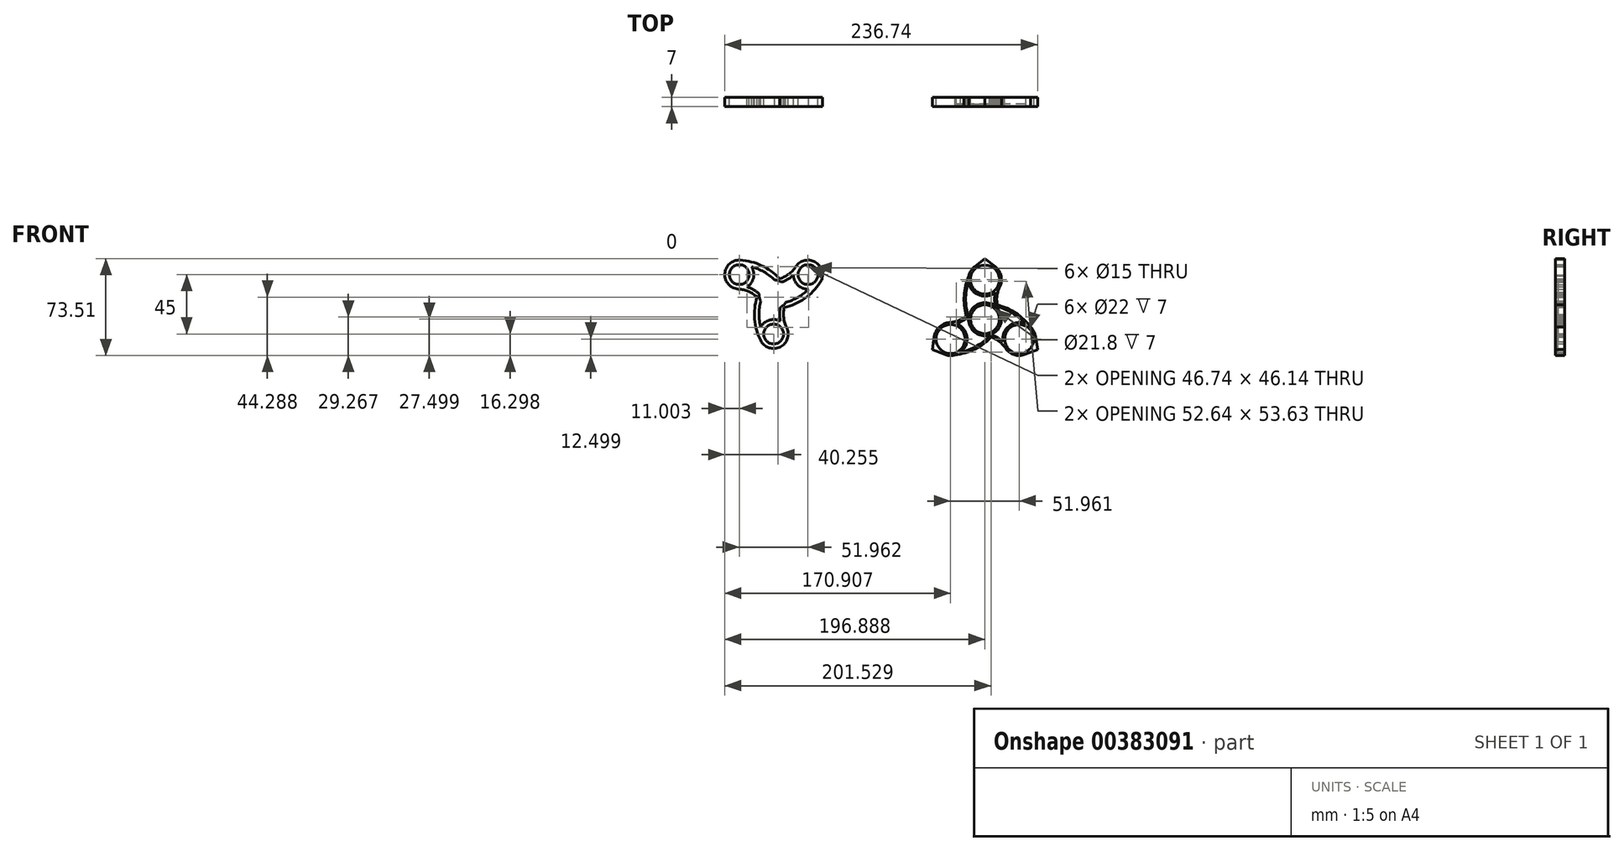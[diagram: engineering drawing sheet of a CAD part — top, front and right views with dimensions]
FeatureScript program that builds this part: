
annotation { "Feature Type Name" : "Feature", "Feature Type Description" : "" }
export const myFeature = defineFeature(function(context is Context, id is Id, definition is map)
    precondition{}
    {
        {
            var Q0;
            Q0=qCreatedBy(makeId("Front.planeOp"),FACE);
            var sketch = newSketch(context, id + "F0", { "sketchPlane" : qUnion([Q0])});
            skCircle(sketch, "E0", {"center": v(-54.28, -12.73) * mm, "radius": 11 * mm});
            skCircle(sketch, "E1", {"center": v(-54.28, -42.73) * mm, "radius": 11 * mm});
            skLineSegment(sketch, "E2", {"start": v(-54.28, 0) * mm, "end": v(-54.28, -55.46) * mm, "construction": true});
            skLineSegment(sketch, "E3", {"start": v(-54.28, -55.46) * mm, "end": v(-24.28, -27.73) * mm, "construction": true});
            skPoint(sketch, "E3.endSnap0", {"position": v(-54.28, -27.73) * mm});
            skLineSegment(sketch, "E4", {"start": v(-24.28, -27.73) * mm, "end": v(-54.28, 0) * mm, "construction": true});
            skLineSegment(sketch, "E5", {"start": v(-24.28, -27.73) * mm, "end": v(-54.28, -12.73) * mm, "construction": true});
            skLineSegment(sketch, "E6", {"start": v(-54.28, -12.73) * mm, "end": v(-87.47, 3.86) * mm, "construction": true});
            skLineSegment(sketch, "E7", {"start": v(-24.28, -27.73) * mm, "end": v(-54.28, -42.73) * mm, "construction": true});
            skLineSegment(sketch, "E8", {"start": v(-54.28, -42.73) * mm, "end": v(-98.2, -64.7) * mm, "construction": true});
            skArc(sketch, "E9", {"start": v(-64.12, -7.81) * mm, "mid": v(-68.82, -27.73) * mm, "end": v(-64.12, -47.65) * mm});
            skArc(sketch, "E10", {"start": v(-64.12, -17.65) * mm, "mid": v(-65.37, -27.73) * mm, "end": v(-64.12, -37.81) * mm});
            skArc(sketch, "E11", {"start": v(-49.17, -22.47) * mm, "mid": v(-49.72, -27.73) * mm, "end": v(-49.17, -32.99) * mm});
            skArc(sketch, "E12", {"start": v(-44.44, -17.65) * mm, "mid": v(-46.82, -27.73) * mm, "end": v(-44.44, -37.81) * mm});
            skCircle(sketch, "E13.1.0", {"center": v(-28.3, 2.27) * mm, "radius": 11 * mm});
            skArc(sketch, "E13.1.1", {"start": v(-45.1, -18.8) * mm, "mid": v(-35.74, -14.84) * mm, "end": v(-27.64, -8.71) * mm});
            skArc(sketch, "E13.1.2", {"start": v(-54.94, -1.75) * mm, "mid": v(-45.02, 1.23) * mm, "end": v(-37.48, 8.33) * mm});
            skArc(sketch, "E13.1.3", {"start": v(-53.62, -23.71) * mm, "mid": v(-34.02, -17.82) * mm, "end": v(-19.12, -3.8) * mm});
            skLineSegment(sketch, "E13.1.4", {"start": v(-65.3, -19.1) * mm, "end": v(-17.27, 8.63) * mm, "construction": true});
            skArc(sketch, "E13.1.5", {"start": v(-48.4, -3.44) * mm, "mid": v(-43.56, -1.28) * mm, "end": v(-39.29, 1.82) * mm});
            skPoint(sketch, "E13.1.7", {"position": v(-41.29, -5.23) * mm});
            skCircle(sketch, "E13.2.0", {"center": v(-80.26, 2.27) * mm, "radius": 11 * mm});
            skArc(sketch, "E13.2.1", {"start": v(-53.62, -1.75) * mm, "mid": v(-61.72, 4.38) * mm, "end": v(-71.08, 8.33) * mm});
            skArc(sketch, "E13.2.2", {"start": v(-63.46, -18.8) * mm, "mid": v(-71, -11.7) * mm, "end": v(-80.92, -8.71) * mm});
            skArc(sketch, "E13.2.3", {"start": v(-45.1, -6.67) * mm, "mid": v(-60, 7.36) * mm, "end": v(-79.6, 13.25) * mm});
            skLineSegment(sketch, "E13.2.4", {"start": v(-43.25, -19.1) * mm, "end": v(-91.28, 8.63) * mm, "construction": true});
            skArc(sketch, "E13.2.5", {"start": v(-65.27, -12.28) * mm, "mid": v(-69.55, -9.18) * mm, "end": v(-74.37, -7.03) * mm});
            skPoint(sketch, "E13.2.7", {"position": v(-67.27, -5.23) * mm});
            skCircle(sketch, "E14", {"center": v(-54.28, -42.73) * mm, "radius": 7.5 * mm});
            skCircle(sketch, "E15", {"center": v(-28.3, 2.27) * mm, "radius": 7.5 * mm});
            skCircle(sketch, "E16", {"center": v(-80.26, 2.27) * mm, "radius": 7.5 * mm});
            skCircle(sketch, "E17", {"center": v(-54.28, -12.73) * mm, "radius": 7.5 * mm});
            skCircle(sketch, "E18", {"center": v(105.63, -31.53) * mm, "radius": 10.9 * mm});
            skArc(sketch, "E19", {"start": v(113.64, -21.94) * mm, "mid": v(100.98, -19.93) * mm, "end": v(93.2, -30.11) * mm});
            skCircle(sketch, "E20", {"center": v(105.63, -1.53) * mm, "radius": 11 * mm});
            skArc(sketch, "E21", {"start": v(93.2, -2.95) * mm, "mid": v(100.98, -13.14) * mm, "end": v(113.64, -11.12) * mm});
            skLineSegment(sketch, "E22", {"start": v(105.63, -56.11) * mm, "end": v(105.63, 45.73) * mm, "construction": true});
            skPoint(sketch, "E23", {"position": v(105.63, -16.53) * mm});
            skLineSegment(sketch, "E24", {"start": v(135.63, -16.53) * mm, "end": v(15.27, 34.9) * mm, "construction": true});
            skLineSegment(sketch, "E25", {"start": v(135.63, -16.53) * mm, "end": v(2.25, -49.47) * mm, "construction": true});
            skPoint(sketch, "E26", {"position": v(93.5, 1.47) * mm});
            skPoint(sketch, "E27", {"position": v(93.5, -34.53) * mm});
            skArc(sketch, "E28", {"start": v(93.5, 1.47) * mm, "mid": v(89.8, -16.53) * mm, "end": v(93.5, -34.53) * mm});
            skArc(sketch, "E29", {"start": v(116.8, -7.12) * mm, "mid": v(114.59, -16.53) * mm, "end": v(116.8, -25.94) * mm});
            skArc(sketch, "E30", {"start": v(115.95, -5.33) * mm, "mid": v(115.35, -6.47) * mm, "end": v(114.8, -7.64) * mm});
            skArc(sketch, "E31.trimOffspring", {"start": v(93.2, -2.95) * mm, "mid": v(91.09, -16.53) * mm, "end": v(93.2, -30.11) * mm});
            skArc(sketch, "E32.trimOffspring", {"start": v(93.5, -34.53) * mm, "mid": v(109.95, -43.26) * mm, "end": v(116.8, -25.94) * mm});
            skArc(sketch, "E33.trimOffspring", {"start": v(113.64, -11.12) * mm, "mid": v(112.99, -16.53) * mm, "end": v(113.64, -21.94) * mm});
            skArc(sketch, "E34.trimOffspring", {"start": v(116.18, -8.22) * mm, "mid": v(110.54, 9.96) * mm, "end": v(93.5, 1.47) * mm});
            skLineSegment(sketch, "E35", {"start": v(116.63, -1.53) * mm, "end": v(118.13, -1.53) * mm});
            skLineSegment(sketch, "E36", {"start": v(113.44, 8.23) * mm, "end": v(105.63, 14.48) * mm});
            skLineSegment(sketch, "E37", {"start": v(105.63, 14.48) * mm, "end": v(97.82, 8.23) * mm});
            skPoint(sketch, "E38.trimOffspring.end.orphan", {"position": v(85.63, -1.53) * mm});
            skLineSegment(sketch, "E39.1.0", {"start": v(67.3, -44.64) * mm, "end": v(65.78, -54.54) * mm});
            skPoint(sketch, "E39.1.1", {"position": v(114.3, -40.54) * mm});
            skPoint(sketch, "E39.1.2", {"position": v(83.11, -58.54) * mm});
            skPoint(sketch, "E39.1.3", {"position": v(89.65, -63.85) * mm});
            skArc(sketch, "E39.1.4", {"start": v(87.08, -56.58) * mm, "mid": v(92.02, -44.75) * mm, "end": v(83.95, -34.8) * mm});
            skCircle(sketch, "E39.1.5", {"center": v(79.65, -46.53) * mm, "radius": 11 * mm});
            skArc(sketch, "E39.1.6", {"start": v(93.31, -29.39) * mm, "mid": v(97.9, -41.35) * mm, "end": v(110.61, -43) * mm});
            skArc(sketch, "E39.1.7", {"start": v(87.08, -56.58) * mm, "mid": v(99.9, -51.62) * mm, "end": v(110.61, -43) * mm});
            skArc(sketch, "E39.1.8", {"start": v(78.9, -34.05) * mm, "mid": v(88.16, -31.27) * mm, "end": v(95.2, -24.64) * mm});
            skArc(sketch, "E39.1.9", {"start": v(80.16, -34.04) * mm, "mid": v(67.24, -48.02) * mm, "end": v(83.11, -58.54) * mm});
            skArc(sketch, "E39.1.10", {"start": v(83.11, -58.54) * mm, "mid": v(100.55, -52.73) * mm, "end": v(114.3, -40.54) * mm});
            skArc(sketch, "E39.1.11", {"start": v(114.3, -40.54) * mm, "mid": v(113.62, -21.92) * mm, "end": v(95.2, -24.64) * mm});
            skLineSegment(sketch, "E39.1.13", {"start": v(65.78, -54.54) * mm, "end": v(75.1, -58.18) * mm});
            skArc(sketch, "E39.1.14", {"start": v(83.95, -34.8) * mm, "mid": v(88.96, -32.66) * mm, "end": v(93.31, -29.39) * mm});
            skPoint(sketch, "E39.1.15", {"position": v(92.64, -39.03) * mm});
            skLineSegment(sketch, "E39.1.16", {"start": v(74.15, -37) * mm, "end": v(73.4, -35.7) * mm});
            skArc(sketch, "E39.1.17", {"start": v(77.78, -35.7) * mm, "mid": v(79.06, -35.65) * mm, "end": v(80.34, -35.53) * mm});
            skLineSegment(sketch, "E39.2.0", {"start": v(136.15, -58.18) * mm, "end": v(145.48, -54.54) * mm});
            skPoint(sketch, "E39.2.1", {"position": v(109.1, -19.52) * mm});
            skPoint(sketch, "E39.2.2", {"position": v(140.28, -37.52) * mm});
            skPoint(sketch, "E39.2.3", {"position": v(141.6, -29.2) * mm});
            skArc(sketch, "E39.2.4", {"start": v(136.6, -35.07) * mm, "mid": v(123.88, -36.7) * mm, "end": v(119.3, -48.67) * mm});
            skCircle(sketch, "E39.2.5", {"center": v(131.6, -46.53) * mm, "radius": 11 * mm});
            skArc(sketch, "E39.2.6", {"start": v(109.93, -43.27) * mm, "mid": v(118, -33.31) * mm, "end": v(113.06, -21.48) * mm});
            skArc(sketch, "E39.2.7", {"start": v(136.6, -35.07) * mm, "mid": v(125.89, -26.44) * mm, "end": v(113.06, -21.48) * mm});
            skArc(sketch, "E39.2.8", {"start": v(121.18, -53.42) * mm, "mid": v(114.14, -46.79) * mm, "end": v(104.88, -44) * mm});
            skArc(sketch, "E39.2.9", {"start": v(120.53, -52.33) * mm, "mid": v(139.1, -56.53) * mm, "end": v(140.28, -37.52) * mm});
            skArc(sketch, "E39.2.10", {"start": v(140.28, -37.52) * mm, "mid": v(126.53, -25.33) * mm, "end": v(109.1, -19.52) * mm});
            skArc(sketch, "E39.2.11", {"start": v(109.1, -19.52) * mm, "mid": v(93.3, -29.4) * mm, "end": v(104.88, -44) * mm});
            skLineSegment(sketch, "E39.2.13", {"start": v(145.48, -54.54) * mm, "end": v(143.97, -44.64) * mm});
            skArc(sketch, "E39.2.14", {"start": v(119.3, -48.67) * mm, "mid": v(114.94, -45.4) * mm, "end": v(109.93, -43.27) * mm});
            skPoint(sketch, "E39.2.15", {"position": v(118.62, -39.03) * mm});
            skLineSegment(sketch, "E39.2.16", {"start": v(126.1, -56.06) * mm, "end": v(125.36, -57.36) * mm});
            skArc(sketch, "E39.2.17", {"start": v(123.15, -53.57) * mm, "mid": v(122.47, -52.48) * mm, "end": v(121.73, -51.43) * mm});
            skSolve(sketch);
        }
        {
            var Q0;
            Q0 = qSketchRegion(id + "F0", true);
            var Q1;
            {var subQ0=sQuery(id+"F0.wireOp",EDGE,"E0");var subQ8=makeQuery(id+"F0.imprint","INTERSECT",VERTEX,{"derivedFrom":[sQuery(id+"F0.wireOp",EDGE,"E11"),subQ0]});Q1=makeQuery(id+"F0.imprint","IMPRINT",FACE,{"disambiguationData":[TD([[makeQuery(id+"F0.imprint","IMPRINT",EDGE,{"disambiguationData":[TD([[subQ8,1.0]])],"derivedFrom":subQ0}),1.0]])]});}
            extrude(context, id + "F1", {"entities" : qUnion([Q0, Q1]), "depth" : 7 * mm, "offsetDistance" : 25 * mm});
        }
        {
            var Q0;
            Q0 = qSketchRegion(id + "F0", true);
            var Q1;
            {var subQ8=sQuery(id+"F0.wireOp",EDGE,"E39.1.6");Q1=makeQuery(id+"F0.imprint","IMPRINT",FACE,{"disambiguationData":[TD([[makeQuery(id+"F0.imprint","IMPRINT",EDGE,{"derivedFrom":subQ8}),1.0]])]});}
            extrude(context, id + "F2", {"entities" : qUnion([Q0, Q1]), "depth" : 7 * mm, "offsetDistance" : 25 * mm});
        }
        {
            var Q0;
            {var subQ5=sQuery(id+"F0.wireOp",EDGE,"E21");Q0=makeQuery(id+"F0.imprint","IMPRINT",FACE,{"disambiguationData":[TD([[makeQuery(id+"F0.imprint","IMPRINT",EDGE,{"derivedFrom":subQ5}),-1.0]])]});}
            var Q1;
            {var subQ1=sQuery(id+"F0.wireOp",EDGE,"E39.1.4");Q1=makeQuery(id+"F0.imprint","IMPRINT",FACE,{"disambiguationData":[TD([[makeQuery(id+"F0.imprint","IMPRINT",EDGE,{"derivedFrom":subQ1}),-1.0]])]});}
            var Q2;
            {var subQ5=sQuery(id+"F0.wireOp",EDGE,"E39.2.4");Q2=makeQuery(id+"F0.imprint","IMPRINT",FACE,{"disambiguationData":[TD([[makeQuery(id+"F0.imprint","IMPRINT",EDGE,{"derivedFrom":subQ5}),-1.0]])]});}
            var Q3;
            {var subQ5=sQuery(id+"F0.wireOp",EDGE,"E39.1.11");Q3=makeQuery(id+"F0.imprint","IMPRINT",FACE,{"disambiguationData":[TD([[makeQuery(id+"F0.imprint","IMPRINT",EDGE,{"derivedFrom":subQ5}),-1.0]])]});}
            var Q4;
            {var subQ0=sQuery(id+"F0.wireOp",EDGE,"E39.2.6");var subQ1=sQuery(id+"F0.wireOp",EDGE,"E29");var subQ2=makeQuery(id+"F0.imprint","INTERSECT",VERTEX,{"derivedFrom":[subQ1,subQ0]});Q4=makeQuery(id+"F0.imprint","IMPRINT",FACE,{"disambiguationData":[TD([[makeQuery(id+"F0.imprint","IMPRINT",EDGE,{"disambiguationData":[TD([[subQ2,1.0]])],"derivedFrom":subQ1}),-1.0]])]});}
            var Q5;
            {var subQ0=sQuery(id+"F0.wireOp",EDGE,"E39.2.6");var subQ1=sQuery(id+"F0.wireOp",EDGE,"E39.1.7");var subQ2=makeQuery(id+"F0.imprint","INTERSECT",VERTEX,{"derivedFrom":[subQ1,subQ0]});Q5=makeQuery(id+"F0.imprint","IMPRINT",FACE,{"disambiguationData":[TD([[makeQuery(id+"F0.imprint","IMPRINT",EDGE,{"disambiguationData":[TD([[subQ2,1.0]])],"derivedFrom":subQ1}),-1.0]])]});}
            var Q6;
            {var subQ0=sQuery(id+"F0.wireOp",EDGE,"E39.1.6");Q6=makeQuery(id+"F0.imprint","IMPRINT",FACE,{"disambiguationData":[TD([[makeQuery(id+"F0.imprint","IMPRINT",EDGE,{"derivedFrom":subQ0}),-1.0]])]});}
            var Q7;
            {var subQ0=sQuery(id+"F0.wireOp",EDGE,"E39.2.11");var subQ1=sQuery(id+"F0.wireOp",EDGE,"E28");var subQ2=makeQuery(id+"F0.imprint","INTERSECT",VERTEX,{"derivedFrom":[subQ1,subQ0]});Q7=makeQuery(id+"F0.imprint","IMPRINT",FACE,{"disambiguationData":[TD([[makeQuery(id+"F0.imprint","IMPRINT",EDGE,{"disambiguationData":[TD([[subQ2,1.0]])],"derivedFrom":subQ1}),1.0]])]});}
            var Q8;
            {var subQ0=sQuery(id+"F0.wireOp",EDGE,"E39.1.8");var subQ1=sQuery(id+"F0.wireOp",EDGE,"E31.trimOffspring");var subQ2=makeQuery(id+"F0.imprint","INTERSECT",VERTEX,{"derivedFrom":[subQ1,subQ0]});Q8=makeQuery(id+"F0.imprint","IMPRINT",FACE,{"disambiguationData":[TD([[makeQuery(id+"F0.imprint","IMPRINT",EDGE,{"disambiguationData":[TD([[subQ2,-1.0]])],"derivedFrom":subQ1}),1.0]])]});}
            extrude(context, id + "F3", {"entities" : qUnion([Q0, Q1, Q2, Q3, Q4, Q5, Q6, Q7, Q8]), "depth" : 5 * mm, "offsetDistance" : 25 * mm});
        }
    });
